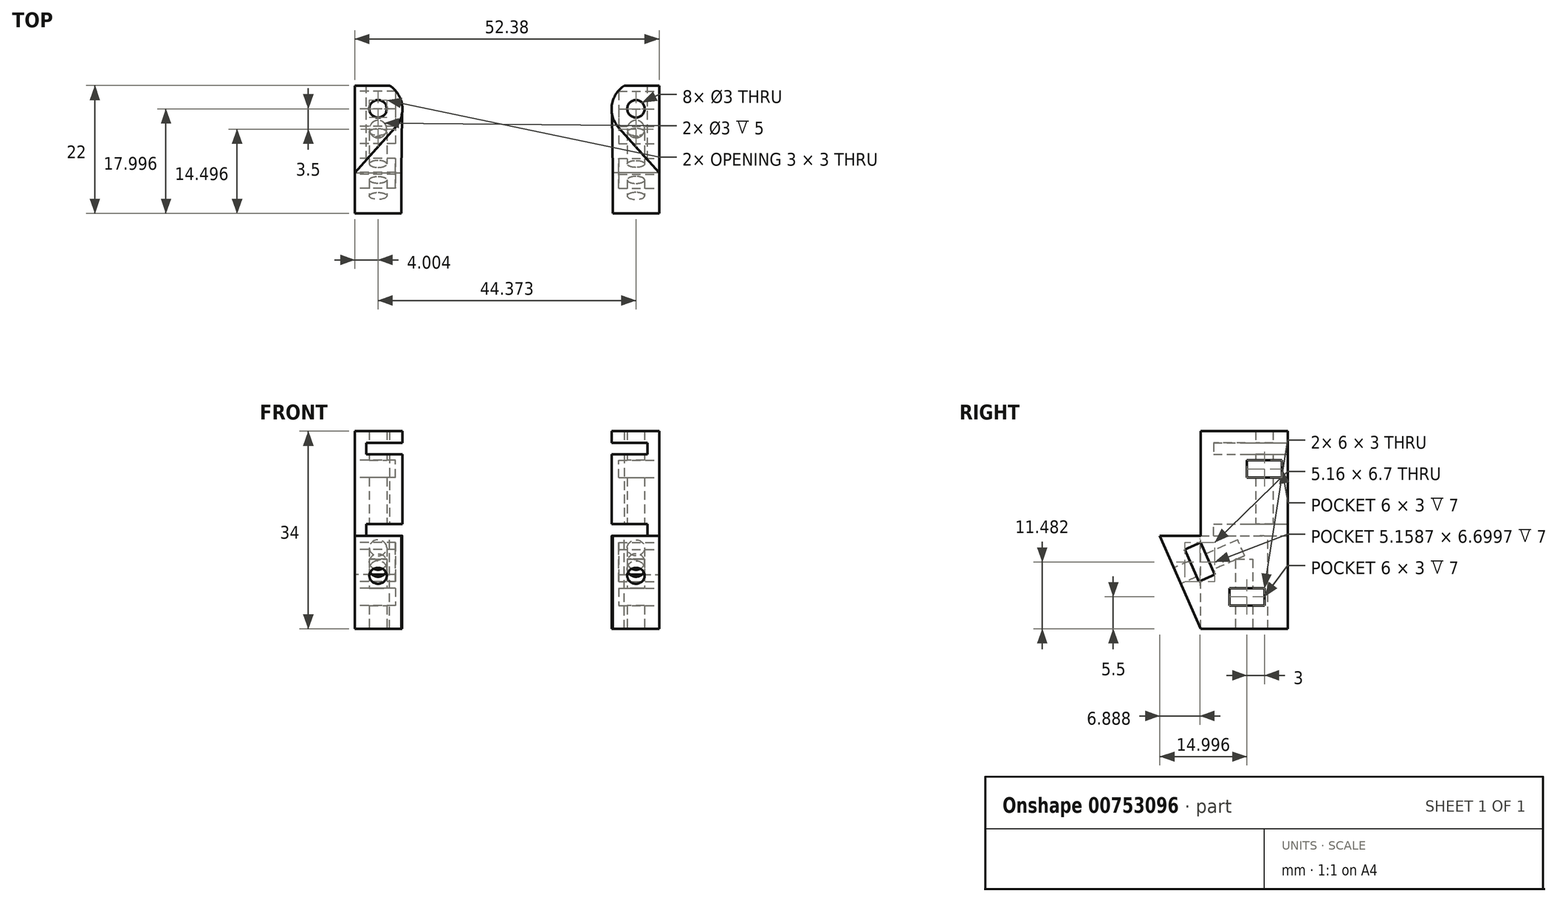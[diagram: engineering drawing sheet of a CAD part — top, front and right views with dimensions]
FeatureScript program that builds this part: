
annotation { "Feature Type Name" : "Feature", "Feature Type Description" : "" }
export const myFeature = defineFeature(function(context is Context, id is Id, definition is map)
    precondition{}
    {
        {
            var Q0;
            Q0=qCreatedBy(makeId("Top.planeOp"),FACE);
            var sketch = newSketch(context, id + "F0", { "sketchPlane" : qUnion([Q0])});
            skLineSegment(sketch, "E0", {"start": v(-26.19, -5.95) * mm, "end": v(-26.19, -20.95) * mm});
            skLineSegment(sketch, "E1", {"start": v(-26.19, -5.95) * mm, "end": v(-20.2, -5.95) * mm});
            skLineSegment(sketch, "E2", {"start": v(-26.19, -20.95) * mm, "end": v(-26.19, -14.95) * mm});
            skLineSegment(sketch, "E3", {"start": v(-26.19, -20.95) * mm, "end": v(-19.23, -13.23) * mm});
            skArc(sketch, "E4", {"start": v(-19.23, -13.23) * mm, "mid": v(-18.04, -9.37) * mm, "end": v(-20.2, -5.95) * mm});
            skCircle(sketch, "E5", {"center": v(-22.19, -9.95) * mm, "radius": 1.5 * mm});
            skSolve(sketch);
        }
        {
            var Q0;
            Q0=makeQuery(id+"F0.imprint","IMPRINT",FACE,{"disambiguationData":[TD([[makeQuery(id+"F0.imprint","IMPRINT",EDGE,{"derivedFrom":sQuery(id+"F0.wireOp",EDGE,"E0")}),1.0]])]});
            extrude(context, id + "F1", {"entities" : qUnion([Q0]), "depth" : 18 * mm, "offsetDistance" : 25 * mm});
        }
        {
            var Q0;
            Q0=makeQuery(id+"F1.opExtrude","SWEPT_FACE",FACE,{"disambiguationData":[OSD([sQuery(id+"F0.wireOp",EDGE,"E0"),sQuery(id+"F0.wireOp",EDGE,"E2")])]});
            var sketch = newSketch(context, id + "F2", { "sketchPlane" : qUnion([Q0])});
            skLineSegment(sketch, "E6", {"start": v(6.95, 13) * mm, "end": v(12.95, 13) * mm});
            skLineSegment(sketch, "E7", {"start": v(12.95, 13) * mm, "end": v(12.95, 10) * mm});
            skLineSegment(sketch, "E8", {"start": v(12.95, 10) * mm, "end": v(6.95, 10) * mm});
            skLineSegment(sketch, "E9", {"start": v(6.95, 10) * mm, "end": v(6.95, 13) * mm});
            skSolve(sketch);
        }
        {
            var Q0;
            Q0=makeQuery(id+"F2.imprint","IMPRINT",FACE,{"disambiguationData":[TD([[makeQuery(id+"F2.imprint","IMPRINT",EDGE,{"derivedFrom":sQuery(id+"F2.wireOp",EDGE,"E6")}),-1.0]])]});
            extrude(context, id + "F3", {"entities" : qUnion([Q0]), "operationType" : NewBodyOperationType.REMOVE, "oppositeDirection" : true, "depth" : 7 * mm, "offsetDistance" : 25 * mm});
        }
        {
            var Q0;
            Q0=makeQuery(id+"F1.opExtrude","CAP_FACE",FACE,{"disambiguationData":[OSD([sQuery(id+"F0.wireOp",EDGE,"E0"),sQuery(id+"F0.wireOp",EDGE,"E1"),sQuery(id+"F0.wireOp",EDGE,"E2"),sQuery(id+"F0.wireOp",EDGE,"E3"),sQuery(id+"F0.wireOp",EDGE,"E4"),sQuery(id+"F0.wireOp",EDGE,"E5")])],"isStart":true});
            var sketch = newSketch(context, id + "F4", { "sketchPlane" : qUnion([Q0])});
            skLineSegment(sketch, "E10", {"start": v(-26.19, 20.95) * mm, "end": v(-18.19, 20.95) * mm});
            skPoint(sketch, "E11.endSnap0", {"position": v(-18.04, 9.37) * mm});
            skLineSegment(sketch, "E12", {"start": v(-26.19, 20.95) * mm, "end": v(-26.19, 5.95) * mm});
            skLineSegment(sketch, "E13", {"start": v(-26.19, 5.95) * mm, "end": v(-20.2, 5.95) * mm});
            skArc(sketch, "E14", {"start": v(-20.2, 5.95) * mm, "mid": v(-18.74, 7.43) * mm, "end": v(-18.04, 9.37) * mm});
            skLineSegment(sketch, "E15", {"start": v(-18.19, 20.95) * mm, "end": v(-18.04, 9.37) * mm});
            skSolve(sketch);
        }
        {
            var Q0;
            Q0=makeQuery(id+"F4.imprint","IMPRINT",FACE,{"disambiguationData":[TD([[makeQuery(id+"F4.imprint","IMPRINT",EDGE,{"derivedFrom":sQuery(id+"F4.wireOp",EDGE,"E12")}),-1.0]])]});
            var Q1;
            {var subQ0=sQuery(id+"F4.wireOp",EDGE,"E10");Q1=makeQuery(id+"F4.imprint","IMPRINT",FACE,{"disambiguationData":[TD([[makeQuery(id+"F4.imprint","IMPRINT",EDGE,{"derivedFrom":subQ0}),-1.0]])]});}
            extrude(context, id + "F5", {"entities" : qUnion([Q0, Q1]), "operationType" : NewBodyOperationType.ADD, "depth" : 16 * mm, "offsetDistance" : 25 * mm});
        }
        {
            var Q0;
            Q0=makeQuery(id+"F5.opExtrude","CAP_FACE",FACE,{"disambiguationData":[OSD([sQuery(id+"F0.wireOp",EDGE,"E5"),sQuery(id+"F4.wireOp",EDGE,"E10"),sQuery(id+"F4.wireOp",EDGE,"E12"),sQuery(id+"F4.wireOp",EDGE,"E13"),sQuery(id+"F4.wireOp",EDGE,"E14"),sQuery(id+"F4.wireOp",EDGE,"E15")])],"isStart":false});
            var sketch = newSketch(context, id + "F6", { "sketchPlane" : qUnion([Q0])});
            skCircle(sketch, "E16", {"center": v(-22.19, 9.95) * mm, "radius": 1.5 * mm});
            skSolve(sketch);
        }
        {
            var Q0;
            Q0=qSketchRegion(id+"F6",true);
            extrude(context, id + "F7", {"entities" : qUnion([Q0]), "operationType" : NewBodyOperationType.ADD, "depth" : -16 * mm, "offsetDistance" : 25 * mm});
        }
        {
            var Q0;
            Q0=makeQuery(id+"F5.boolean.opBoolean","MERGE",FACE,{"derivedFrom":[makeQuery(id+"F1.opExtrude","SWEPT_FACE",FACE,{"disambiguationData":[OSD([sQuery(id+"F0.wireOp",EDGE,"E0"),sQuery(id+"F0.wireOp",EDGE,"E2")])]}),makeQuery(id+"F5.opExtrude","SWEPT_FACE",FACE,{"disambiguationData":[OSD([sQuery(id+"F4.wireOp",EDGE,"E12")])]})]});
            var sketch = newSketch(context, id + "F8", { "sketchPlane" : qUnion([Q0])});
            skLineSegment(sketch, "E17", {"start": v(20.95, -16) * mm, "end": v(20.95, 0) * mm});
            skLineSegment(sketch, "E18", {"start": v(20.95, 0) * mm, "end": v(27.95, 0) * mm});
            skLineSegment(sketch, "E19", {"start": v(27.95, 0) * mm, "end": v(20.95, -16) * mm});
            skSolve(sketch);
        }
        {
            var Q0;
            Q0=makeQuery(id+"F8.imprint","IMPRINT",FACE,{"disambiguationData":[TD([[makeQuery(id+"F8.imprint","IMPRINT",EDGE,{"derivedFrom":sQuery(id+"F8.wireOp",EDGE,"E17")}),-1.0]])]});
            extrude(context, id + "F9", {"entities" : qUnion([Q0]), "operationType" : NewBodyOperationType.ADD, "depth" : -8 * mm, "offsetDistance" : 25 * mm});
        }
        {
            var Q0;
            Q0=makeQuery(id+"F9.boolean.opBoolean","MERGE",FACE,{"derivedFrom":[makeQuery(id+"F5.boolean.opBoolean","MERGE",FACE,{"derivedFrom":[makeQuery(id+"F1.opExtrude","SWEPT_FACE",FACE,{"disambiguationData":[OSD([sQuery(id+"F0.wireOp",EDGE,"E0"),sQuery(id+"F0.wireOp",EDGE,"E2")])]}),makeQuery(id+"F5.opExtrude","SWEPT_FACE",FACE,{"disambiguationData":[OSD([sQuery(id+"F4.wireOp",EDGE,"E12")])]})]}),makeQuery(id+"F9.opExtrude","CAP_FACE",FACE,{"disambiguationData":[OSD([sQuery(id+"F8.wireOp",EDGE,"E17"),sQuery(id+"F8.wireOp",EDGE,"E18"),sQuery(id+"F8.wireOp",EDGE,"E19")])],"isStart":true})]});
            var sketch = newSketch(context, id + "F10", { "sketchPlane" : qUnion([Q0])});
            skLineSegment(sketch, "E20", {"start": v(23.64, -2.37) * mm, "end": v(20.9, -1.17) * mm});
            skLineSegment(sketch, "E21", {"start": v(20.9, -1.17) * mm, "end": v(18.48, -6.66) * mm});
            skLineSegment(sketch, "E22", {"start": v(18.48, -6.66) * mm, "end": v(21.23, -7.87) * mm});
            skLineSegment(sketch, "E23", {"start": v(21.23, -7.87) * mm, "end": v(23.64, -2.37) * mm});
            skSolve(sketch);
        }
        {
            var Q0;
            Q0=makeQuery(id+"F10.imprint","IMPRINT",FACE,{"disambiguationData":[TD([[makeQuery(id+"F10.imprint","IMPRINT",EDGE,{"derivedFrom":sQuery(id+"F10.wireOp",EDGE,"E20")}),1.0]])]});
            extrude(context, id + "F11", {"entities" : qUnion([Q0]), "operationType" : NewBodyOperationType.REMOVE, "oppositeDirection" : true, "depth" : 7 * mm, "offsetDistance" : 25 * mm});
        }
        {
            var Q0;
            Q0=makeQuery(id+"F9.opExtrude","SWEPT_FACE",FACE,{"disambiguationData":[OSD([sQuery(id+"F8.wireOp",EDGE,"E19")])]});
            var sketch = newSketch(context, id + "F12", { "sketchPlane" : qUnion([Q0])});
            skCircle(sketch, "E24", {"center": v(-22.19, 3.7) * mm, "radius": 1.5 * mm});
            skSolve(sketch);
        }
        {
            var Q0;
            Q0=makeQuery(id+"F12.imprint","IMPRINT",FACE,{"disambiguationData":[TD([[makeQuery(id+"F12.imprint","IMPRINT",EDGE,{"derivedFrom":sQuery(id+"F12.wireOp",EDGE,"E24")}),1.0]])]});
            extrude(context, id + "F13", {"entities" : qUnion([Q0]), "operationType" : NewBodyOperationType.REMOVE, "oppositeDirection" : true, "depth" : 12 * mm, "offsetDistance" : 25 * mm});
        }
        {
            var Q0;
            Q0=makeQuery(id+"F9.boolean.opBoolean","MERGE",FACE,{"derivedFrom":[makeQuery(id+"F5.boolean.opBoolean","MERGE",FACE,{"derivedFrom":[makeQuery(id+"F1.opExtrude","SWEPT_FACE",FACE,{"disambiguationData":[OSD([sQuery(id+"F0.wireOp",EDGE,"E0"),sQuery(id+"F0.wireOp",EDGE,"E2")])]}),makeQuery(id+"F5.opExtrude","SWEPT_FACE",FACE,{"disambiguationData":[OSD([sQuery(id+"F4.wireOp",EDGE,"E12")])]})]}),makeQuery(id+"F9.opExtrude","CAP_FACE",FACE,{"disambiguationData":[OSD([sQuery(id+"F8.wireOp",EDGE,"E17"),sQuery(id+"F8.wireOp",EDGE,"E18"),sQuery(id+"F8.wireOp",EDGE,"E19")])],"isStart":true})]});
            var sketch = newSketch(context, id + "F14", { "sketchPlane" : qUnion([Q0])});
            skLineSegment(sketch, "E25", {"start": v(9.95, -12) * mm, "end": v(15.95, -12) * mm});
            skLineSegment(sketch, "E26", {"start": v(15.95, -12) * mm, "end": v(15.95, -9) * mm});
            skLineSegment(sketch, "E27", {"start": v(15.95, -9) * mm, "end": v(9.95, -9) * mm});
            skLineSegment(sketch, "E28", {"start": v(9.95, -9) * mm, "end": v(9.95, -12) * mm});
            skSolve(sketch);
        }
        {
            var Q0;
            Q0=makeQuery(id+"F14.imprint","IMPRINT",FACE,{"disambiguationData":[TD([[makeQuery(id+"F14.imprint","IMPRINT",EDGE,{"derivedFrom":sQuery(id+"F14.wireOp",EDGE,"E25")}),1.0]])]});
            extrude(context, id + "F15", {"entities" : qUnion([Q0]), "operationType" : NewBodyOperationType.REMOVE, "oppositeDirection" : true, "depth" : 7 * mm, "offsetDistance" : 25 * mm});
        }
        {
            var Q0;
            Q0=makeQuery(id+"F7.boolean.opBoolean","MERGE",FACE,{"derivedFrom":[makeQuery(id+"F5.opExtrude","CAP_FACE",FACE,{"disambiguationData":[OSD([sQuery(id+"F0.wireOp",EDGE,"E5"),sQuery(id+"F4.wireOp",EDGE,"E10"),sQuery(id+"F4.wireOp",EDGE,"E12"),sQuery(id+"F4.wireOp",EDGE,"E13"),sQuery(id+"F4.wireOp",EDGE,"E14"),sQuery(id+"F4.wireOp",EDGE,"E15")])],"isStart":false}),makeQuery(id+"F7.opExtrude","CAP_FACE",FACE,{"disambiguationData":[OSD([sQuery(id+"F6.wireOp",EDGE,"E16")])],"isStart":true})]});
            var sketch = newSketch(context, id + "F16", { "sketchPlane" : qUnion([Q0])});
            skCircle(sketch, "E29", {"center": v(-22.19, 13.45) * mm, "radius": 1.5 * mm});
            skSolve(sketch);
        }
        {
            var Q0;
            Q0=makeQuery(id+"F16.imprint","IMPRINT",FACE,{"disambiguationData":[TD([[makeQuery(id+"F16.imprint","IMPRINT",EDGE,{"derivedFrom":sQuery(id+"F16.wireOp",EDGE,"E29")}),1.0]])]});
            extrude(context, id + "F17", {"entities" : qUnion([Q0]), "operationType" : NewBodyOperationType.REMOVE, "oppositeDirection" : true, "depth" : 12 * mm, "offsetDistance" : 25 * mm});
        }
        {
            var Q0;
            Q0=makeQuery(id+"F5.boolean.opBoolean","MERGE",FACE,{"derivedFrom":[makeQuery(id+"F1.opExtrude","SWEPT_FACE",FACE,{"disambiguationData":[OSD([sQuery(id+"F0.wireOp",EDGE,"E1")])]}),makeQuery(id+"F5.opExtrude","SWEPT_FACE",FACE,{"disambiguationData":[OSD([sQuery(id+"F4.wireOp",EDGE,"E13")])]})]});
            var sketch = newSketch(context, id + "F18", { "sketchPlane" : qUnion([Q0])});
            skLineSegment(sketch, "E30", {"start": v(26.19, 0) * mm, "end": v(24.19, 0) * mm});
            skLineSegment(sketch, "E31", {"start": v(24.19, 0) * mm, "end": v(24.19, 2) * mm});
            skLineSegment(sketch, "E32", {"start": v(24.19, 2) * mm, "end": v(26.19, 2) * mm});
            skLineSegment(sketch, "E33", {"start": v(24.19, 2) * mm, "end": v(20.2, 2) * mm});
            skLineSegment(sketch, "E34", {"start": v(20.2, 2) * mm, "end": v(20.2, 0) * mm});
            skLineSegment(sketch, "E35", {"start": v(20.2, 0) * mm, "end": v(24.19, 0) * mm});
            skSolve(sketch);
        }
        {
            var Q0;
            Q0=makeQuery(id+"F18.imprint","IMPRINT",FACE,{"disambiguationData":[TD([[makeQuery(id+"F18.imprint","IMPRINT",EDGE,{"derivedFrom":sQuery(id+"F18.wireOp",EDGE,"E31")}),1.0]])]});
            extrude(context, id + "F19", {"entities" : qUnion([Q0]), "operationType" : NewBodyOperationType.REMOVE, "oppositeDirection" : true, "depth" : 25 * mm, "offsetDistance" : 25 * mm});
        }
        {
            var Q0;
            Q0=makeQuery(id+"F19.boolean.opBoolean","COPY",FACE,{"derivedFrom":makeQuery(id+"F19.opExtrude","SWEPT_FACE",FACE,{"disambiguationData":[OSD([sQuery(id+"F18.wireOp",EDGE,"E34")])]})});
            extrude(context, id + "F20", {"entities" : qUnion([Q0]), "operationType" : NewBodyOperationType.REMOVE, "oppositeDirection" : true, "depth" : 25 * mm, "offsetDistance" : 25 * mm});
        }
        {
            var Q0;
            Q0=makeQuery(id+"F5.boolean.opBoolean","MERGE",FACE,{"derivedFrom":[makeQuery(id+"F1.opExtrude","SWEPT_FACE",FACE,{"disambiguationData":[OSD([sQuery(id+"F0.wireOp",EDGE,"E1")])]}),makeQuery(id+"F5.opExtrude","SWEPT_FACE",FACE,{"disambiguationData":[OSD([sQuery(id+"F4.wireOp",EDGE,"E13")])]})]});
            var sketch = newSketch(context, id + "F21", { "sketchPlane" : qUnion([Q0])});
            skLineSegment(sketch, "E36", {"start": v(26.19, 18) * mm, "end": v(26.19, 16) * mm});
            skLineSegment(sketch, "E37", {"start": v(26.19, 16) * mm, "end": v(26.19, 14) * mm});
            skLineSegment(sketch, "E38", {"start": v(26.19, 14) * mm, "end": v(24.19, 14) * mm});
            skLineSegment(sketch, "E39", {"start": v(24.19, 14) * mm, "end": v(20.2, 14) * mm});
            skLineSegment(sketch, "E40", {"start": v(20.2, 14) * mm, "end": v(20.2, 16) * mm});
            skLineSegment(sketch, "E41", {"start": v(20.2, 16) * mm, "end": v(26.19, 16) * mm});
            skLineSegment(sketch, "E42", {"start": v(24.19, 16) * mm, "end": v(24.19, 14) * mm});
            skSolve(sketch);
        }
        {
            var Q0;
            Q0=makeQuery(id+"F21.imprint","IMPRINT",FACE,{"disambiguationData":[TD([[makeQuery(id+"F21.imprint","IMPRINT",EDGE,{"derivedFrom":sQuery(id+"F21.wireOp",EDGE,"E39")}),-1.0]])]});
            extrude(context, id + "F22", {"entities" : qUnion([Q0]), "operationType" : NewBodyOperationType.REMOVE, "oppositeDirection" : true, "depth" : 25 * mm, "offsetDistance" : 25 * mm});
        }
        {
            var Q0;
            Q0=makeQuery(id+"F22.boolean.opBoolean","COPY",FACE,{"derivedFrom":makeQuery(id+"F22.opExtrude","SWEPT_FACE",FACE,{"disambiguationData":[OSD([sQuery(id+"F21.wireOp",EDGE,"E40")])]})});
            extrude(context, id + "F23", {"entities" : qUnion([Q0]), "operationType" : NewBodyOperationType.REMOVE, "oppositeDirection" : true, "depth" : 25 * mm, "offsetDistance" : 25 * mm});
        }
        {
            var Q0;
            Q0=makeQuery(id+"F1.opExtrude","SWEPT_BODY",BODY,{"disambiguationData":[OSD([sQuery(id+"F0.wireOp",EDGE,"E0"),sQuery(id+"F0.wireOp",EDGE,"E1"),sQuery(id+"F0.wireOp",EDGE,"E2"),sQuery(id+"F0.wireOp",EDGE,"E3"),sQuery(id+"F0.wireOp",EDGE,"E4"),sQuery(id+"F0.wireOp",EDGE,"E5")])]});
            var Q1;
            Q1=qCreatedBy(makeId("Right.planeOp"),FACE);
            mirror(context, id + "F24", {"entities" : qUnion([Q0]), "mirrorPlane" : qUnion([Q1])});
        }
    });
